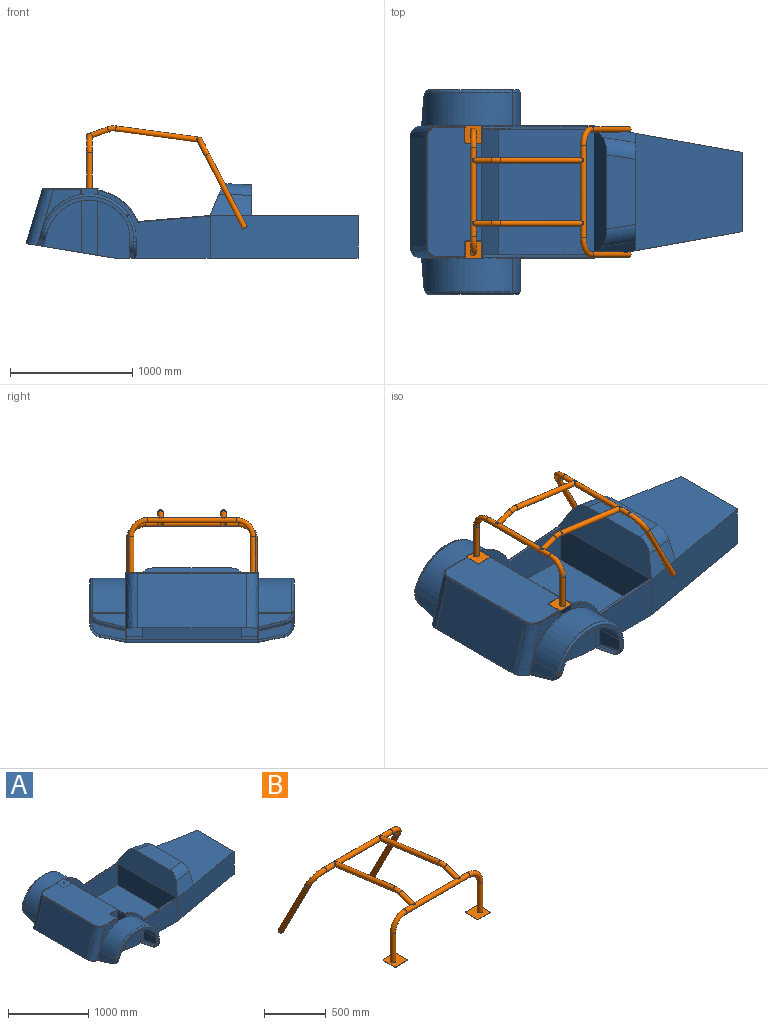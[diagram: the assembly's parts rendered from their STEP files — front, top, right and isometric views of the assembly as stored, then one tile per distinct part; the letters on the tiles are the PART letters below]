
ASSEMBLY  parts=2 mates=1
PART A: 180 faces, bbox 2842.1x1692.5x1027.8 mm
  f0: plane 10x10mm, normal (-1,0,0), area 21.5mm2, adj f1,f4,f161
  f1: plane 1374.1x570mm, normal (0,1,0), area 236734.2mm2, adj f0,f3,f4,f5,f11,f12,f15,f17
  f2: cylinder r=2.5mm len=25mm, axis (0,0,1), area 392.7mm2, adj f3,f4
  f3: plane 135x135mm, normal (0,0,-1), area 18205.4mm2, adj f1,f2,f5,f137,f138
  f4: plane 1070x442.56mm, normal (0,0,1), area 450483.3mm2, adj f0,f1,f2,f136,f139,f140,f161,f162
  f5: plane 498.97x135mm, normal (1,0,0), area 67361.3mm2, adj f1,f3,f16,f20,f138
  f6: cylinder r=350mm len=617.19mm, axis (0,1,0), area 3102.4mm2, adj f7,f10,f19,f30,f44,f57
  f7: cylinder r=363.11mm len=6.49mm, axis (0,1,0), area 32mm2, adj f6,f8,f19,f44
  f8: cylinder r=270mm len=155.14mm, axis (0,1,0), area 661.1mm2, adj f7,f14,f19,f44
  f9: plane 274.45x116.01mm, normal (-0.96,0,0.29), area 23220.8mm2, adj f15,f31,f32,f145
  f10: plane 289.56x128.37mm, normal (0.96,0,-0.29), area 1360.6mm2, adj f6,f16,f24,f29,f30,f41,f56,f57
  f11: plane 1985x1090mm, normal (0,0,-1), area 1885188.1mm2, adj f1,f16,f24,f26,f28,f61,f97,f99
  f12: plane 275x151.07mm, normal (1,0,0), area 33172.1mm2, adj f1,f13,f17,f27,f28
  f13: cylinder r=20mm len=30.73mm, axis (0,0,-1), area 965.5mm2, adj f12,f19,f23,f27
  f14: plane 290x170.47mm, normal (-1,0,0), area 1514.6mm2, adj f8,f19,f24,f25,f26,f44,f52,f53
  f15: cylinder r=400mm len=705.36mm, axis (0,-1,0), area 243757.5mm2, adj f1,f9,f18,f20,f21,f33
  f16: plane 1142.4x730mm, normal (-0.16,0,-0.99), area 20183mm2, adj f5,f10,f11,f20,f24,f29,f31,f81
  f17: cylinder r=320mm len=275mm, axis (0,-1,0), area 53866.2mm2, adj f1,f12,f18,f23
  f18: cylinder r=413.11mm len=275mm, axis (0,-1,0), area 2502.2mm2, adj f1,f15,f17,f22
  f19: plane 726.81x365mm, normal (0,1,0), area 30389.1mm2, adj f6,f7,f8,f13,f14,f21,f22,f23
  f20: plane 500.9x135mm, normal (0,-1,0), area 65864mm2, adj f5,f15,f16,f137
  f21: torus R=380mm, axis (0,1,0), area 27036.4mm2, adj f15,f19,f22,f33
  f22: torus R=393.11mm, axis (0,1,0), area 280.8mm2, adj f18,f19,f21,f23
  f23: torus R=300mm, axis (0,1,0), area 6013.9mm2, adj f13,f17,f19,f22
  f24: plane 709.39x474.73mm, normal (0,1,0), area 251490.4mm2, adj f10,f11,f14,f16,f35,f39,f49,f50
  f25: cylinder r=100mm len=98.08mm, axis (-1,0,0), area 4123.6mm2, adj f14,f19,f26,f27
  f26: plane 209.5x41.65mm, normal (0,0.2,-0.98), area 6408.1mm2, adj f11,f14,f25,f28
  f27: torus R=80mm, axis (1,0,0), area 4004.4mm2, adj f12,f13,f25,f28
  f28: cylinder r=20mm len=218.21mm, axis (0,0.98,0.2), area 6804mm2, adj f1,f11,f12,f26,f27
  f29: plane 203.47x52.98mm, normal (-0.28,0.24,-0.93), area 6044.2mm2, adj f10,f16,f30,f31
  f30: cylinder r=100mm len=101.65mm, axis (0.96,0,-0.29), area 3986.8mm2, adj f6,f10,f19,f29,f32,f33
  f31: cylinder r=20mm len=223.14mm, axis (0.07,0.97,0.23), area 6930.7mm2, adj f9,f16,f29,f32,f141
  f32: torus R=80mm, axis (-0.96,0,0.29), area 3529.2mm2, adj f9,f30,f31,f33
  f33: bspline ~41x29.86mm, area 352.5mm2, adj f15,f21,f30,f32
  f34: plane 270.45x115.06mm, normal (0.96,0,-0.29), area 22738.3mm2, adj f40,f45,f58,f59
  f35: plane 124.5x37.35mm, normal (-0.96,0,0.29), area 130mm2, adj f24,f41,f45,f51
  f36: plane 31.94x0.61mm, normal (0,0,1), area 19mm2, adj f39,f45,f53,f55
  f37: plane 271x150.28mm, normal (-1,0,0), area 32569.4mm2, adj f38,f42,f45,f54,f55
  f38: cylinder r=16mm len=30.73mm, axis (0,0,-1), area 772.4mm2, adj f37,f44,f48,f54
  f39: plane 166.47x1mm, normal (1,0,0), area 166.5mm2, adj f24,f36,f45,f49,f53
  f40: cylinder r=396mm len=698.31mm, axis (0,-1,0), area 237809.8mm2, adj f34,f43,f45,f46,f60
  f41: plane 37.09x26.85mm, normal (0.16,0,0.99), area 624.6mm2, adj f10,f35,f45,f56,f58
  f42: cylinder r=316mm len=271mm, axis (0,-1,0), area 52419.2mm2, adj f37,f43,f45,f48
  f43: cylinder r=409.11mm len=271mm, axis (0,-1,0), area 2442mm2, adj f40,f42,f45,f47
  f44: plane 726.81x365mm, normal (0,-1,0), area 30389.1mm2, adj f6,f7,f8,f14,f38,f46,f47,f48
  f45: plane 796.18x516.73mm, normal (0,1,0), area 60341.2mm2, adj f34,f35,f36,f37,f39,f40,f41,f42
  f46: torus R=380mm, axis (0,1,0), area 21488.9mm2, adj f40,f44,f47,f60
  f47: torus R=393.11mm, axis (0,1,0), area 223.3mm2, adj f43,f44,f46,f48
  f48: torus R=300mm, axis (0,1,0), area 4771.9mm2, adj f38,f42,f44,f47
  f49: cylinder r=270mm len=155.14mm, axis (0,1,0), area 165.3mm2, adj f24,f39,f45,f50
  f50: cylinder r=363.11mm len=6.49mm, axis (0,1,0), area 8mm2, adj f24,f45,f49,f51
  f51: cylinder r=350mm len=617.19mm, axis (0,1,0), area 775.6mm2, adj f24,f35,f45,f50
  f52: cylinder r=96mm len=94.16mm, axis (-1,0,0), area 3958.6mm2, adj f14,f44,f53,f54
  f53: plane 209.11x41.58mm, normal (0,-0.2,0.98), area 6396.2mm2, adj f14,f36,f39,f52,f55
  f54: torus R=80mm, axis (1,0,0), area 3115.5mm2, adj f37,f38,f52,f55
  f55: cylinder r=16mm len=212.82mm, axis (0,0.98,0.2), area 5344.2mm2, adj f36,f37,f45,f53,f54
  f56: plane 202.86x52.84mm, normal (0.28,-0.24,0.93), area 6025.4mm2, adj f10,f41,f57,f58
  f57: cylinder r=96mm len=97.93mm, axis (0.96,0,-0.29), area 3827.3mm2, adj f6,f10,f44,f56,f59,f60
  f58: cylinder r=16mm len=217.4mm, axis (0.07,0.97,0.23), area 5451mm2, adj f34,f41,f45,f56,f59
  f59: torus R=80mm, axis (-0.96,0,0.29), area 2745.8mm2, adj f34,f57,f58,f60
  f60: bspline ~38.29x25.61mm, area 272.9mm2, adj f40,f46,f57,f59
  f61: plane 920x570mm, normal (0,-1,0), area 208720.6mm2, adj f11,f73,f74,f75,f76,f87,f90,f91
  f62: cylinder r=440mm len=280.56mm, axis (0,-1,0), area 6757.6mm2, adj f63,f71,f76,f136
  f63: cylinder r=453.11mm len=20mm, axis (0,-1,0), area 199.6mm2, adj f62,f64,f71,f75
  f64: cylinder r=360mm len=77.32mm, axis (0,-1,0), area 1757.2mm2, adj f63,f65,f71,f74
  f65: plane 589.44x50mm, normal (-0.08,0,1), area 11831mm2, adj f64,f71,f73,f174
  f66: cylinder r=440mm len=280.56mm, axis (0,-1,0), area 6757.6mm2, adj f67,f72,f77,f136
  f67: cylinder r=453.11mm len=20mm, axis (0,-1,0), area 199.6mm2, adj f66,f68,f72,f78
  f68: cylinder r=360mm len=77.32mm, axis (0,-1,0), area 1757.2mm2, adj f67,f69,f72,f80
  f69: plane 589.44x50mm, normal (-0.08,0,1), area 11831mm2, adj f68,f72,f79,f174
  f70: plane 1030x781.36mm, normal (0,0,1), area 804800.4mm2, adj f71,f72,f136,f166
  f71: plane 917.07x533.49mm, normal (0,1,0), area 288293.1mm2, adj f62,f63,f64,f65,f70,f136,f166
  f72: plane 917.07x533.49mm, normal (0,-1,0), area 288293.1mm2, adj f66,f67,f68,f69,f70,f136,f166
  f73: cylinder r=5mm len=593.62mm, axis (1,0,0.08), area 4655.6mm2, adj f61,f65,f74,f169
  f74: torus R=355mm, axis (0,1,0), area 697.3mm2, adj f61,f64,f73,f75
  f75: torus R=448.11mm, axis (0,1,0), area 78.1mm2, adj f61,f63,f74,f76
  f76: torus R=435mm, axis (0,1,0), area 2636.4mm2, adj f61,f62,f75,f136
  f77: torus R=435mm, axis (0,1,0), area 2636.4mm2, adj f1,f66,f78,f136
  f78: torus R=448.11mm, axis (0,1,0), area 78.1mm2, adj f1,f67,f77,f80
  f79: cylinder r=5mm len=593.62mm, axis (-1,0,-0.08), area 4655.6mm2, adj f1,f69,f80,f167
  f80: torus R=355mm, axis (0,1,0), area 697.3mm2, adj f1,f68,f78,f79
  f81: plane 500.9x135mm, normal (0,1,0), area 65864mm2, adj f16,f90,f135,f140
  f82: cylinder r=350mm len=617.19mm, axis (0,-1,0), area 3102.4mm2, adj f83,f86,f93,f103,f117,f130
  f83: cylinder r=363.11mm len=6.49mm, axis (0,-1,0), area 32mm2, adj f82,f84,f93,f117
  f84: cylinder r=270mm len=155.14mm, axis (0,-1,0), area 661.1mm2, adj f83,f89,f93,f117
  f85: plane 274.45x116.01mm, normal (-0.96,0,0.29), area 23220.8mm2, adj f90,f104,f105,f143
  f86: plane 289.56x128.37mm, normal (0.96,0,-0.29), area 1360.6mm2, adj f16,f82,f97,f102,f103,f114,f129,f130
  f87: plane 275x151.07mm, normal (1,0,0), area 33172.1mm2, adj f61,f88,f91,f100,f101
  f88: cylinder r=20mm len=30.73mm, axis (0,0,-1), area 965.5mm2, adj f87,f93,f96,f100
  f89: plane 290x170.47mm, normal (-1,0,0), area 1514.6mm2, adj f84,f93,f97,f98,f99,f117,f125,f126
  f90: cylinder r=400mm len=705.36mm, axis (0,1,0), area 243757.5mm2, adj f61,f81,f85,f92,f94,f106,f134
  f91: cylinder r=320mm len=275mm, axis (0,1,0), area 53866.2mm2, adj f61,f87,f92,f96
  f92: cylinder r=413.11mm len=275mm, axis (0,1,0), area 2502.2mm2, adj f61,f90,f91,f95
  f93: plane 726.81x365mm, normal (0,-1,0), area 30389.1mm2, adj f82,f83,f84,f88,f89,f94,f95,f96
  f94: torus R=380mm, axis (0,-1,0), area 27036.4mm2, adj f90,f93,f95,f106
  f95: torus R=393.11mm, axis (0,-1,0), area 280.8mm2, adj f92,f93,f94,f96
  f96: torus R=300mm, axis (0,-1,0), area 6013.9mm2, adj f88,f91,f93,f95
  f97: plane 709.39x474.73mm, normal (0,-1,0), area 251490.4mm2, adj f11,f16,f86,f89,f108,f112,f122,f123
  f98: cylinder r=100mm len=98.08mm, axis (-1,0,0), area 4123.6mm2, adj f89,f93,f99,f100
  f99: plane 209.5x41.65mm, normal (0,-0.2,-0.98), area 6408.1mm2, adj f11,f89,f98,f101
  f100: torus R=80mm, axis (1,0,0), area 4004.4mm2, adj f87,f88,f98,f101
  f101: cylinder r=20mm len=218.21mm, axis (0,-0.98,0.2), area 6804mm2, adj f11,f61,f87,f99,f100
  f102: plane 203.47x52.98mm, normal (-0.28,-0.24,-0.93), area 6044.2mm2, adj f16,f86,f103,f104
  f103: cylinder r=100mm len=101.65mm, axis (0.96,0,-0.29), area 3986.8mm2, adj f82,f86,f93,f102,f105,f106
  f104: cylinder r=20mm len=223.14mm, axis (0.07,-0.97,0.23), area 6930.7mm2, adj f16,f85,f102,f105,f142
  f105: torus R=80mm, axis (-0.96,0,0.29), area 3529.2mm2, adj f85,f103,f104,f106
  f106: bspline ~41x29.86mm, area 352.5mm2, adj f90,f94,f103,f105
  f107: plane 270.45x115.06mm, normal (0.96,0,-0.29), area 22738.3mm2, adj f113,f118,f131,f132
  f108: plane 124.5x37.35mm, normal (-0.96,0,0.29), area 130mm2, adj f97,f114,f118,f124
  f109: plane 31.94x0.61mm, normal (0,0,1), area 19mm2, adj f112,f118,f126,f128
  f110: plane 271x150.28mm, normal (-1,0,0), area 32569.4mm2, adj f111,f115,f118,f127,f128
  f111: cylinder r=16mm len=30.73mm, axis (0,0,-1), area 772.4mm2, adj f110,f117,f121,f127
  f112: plane 166.47x1mm, normal (1,0,0), area 166.5mm2, adj f97,f109,f118,f122,f126
  f113: cylinder r=396mm len=698.31mm, axis (0,1,0), area 237809.8mm2, adj f107,f116,f118,f119,f133
  f114: plane 37.09x26.85mm, normal (0.16,0,0.99), area 624.6mm2, adj f86,f108,f118,f129,f131
  f115: cylinder r=316mm len=271mm, axis (0,1,0), area 52419.2mm2, adj f110,f116,f118,f121
  f116: cylinder r=409.11mm len=271mm, axis (0,1,0), area 2442mm2, adj f113,f115,f118,f120
  f117: plane 726.81x365mm, normal (0,1,0), area 30389.1mm2, adj f82,f83,f84,f89,f111,f119,f120,f121
  f118: plane 796.18x516.73mm, normal (0,-1,0), area 60341.2mm2, adj f107,f108,f109,f110,f112,f113,f114,f115
  f119: torus R=380mm, axis (0,-1,0), area 21488.9mm2, adj f113,f117,f120,f133
  f120: torus R=393.11mm, axis (0,-1,0), area 223.3mm2, adj f116,f117,f119,f121
  f121: torus R=300mm, axis (0,-1,0), area 4771.9mm2, adj f111,f115,f117,f120
  f122: cylinder r=270mm len=155.14mm, axis (0,-1,0), area 165.3mm2, adj f97,f112,f118,f123
  f123: cylinder r=363.11mm len=6.49mm, axis (0,-1,0), area 8mm2, adj f97,f118,f122,f124
  f124: cylinder r=350mm len=617.19mm, axis (0,-1,0), area 775.6mm2, adj f97,f108,f118,f123
  f125: cylinder r=96mm len=94.16mm, axis (-1,0,0), area 3958.6mm2, adj f89,f117,f126,f127
  f126: plane 209.11x41.58mm, normal (0,0.2,0.98), area 6396.2mm2, adj f89,f109,f112,f125,f128
  f127: torus R=80mm, axis (1,0,0), area 3115.5mm2, adj f110,f111,f125,f128
  f128: cylinder r=16mm len=212.82mm, axis (0,-0.98,0.2), area 5344.2mm2, adj f109,f110,f118,f126,f127
  f129: plane 202.86x52.84mm, normal (0.28,0.24,0.93), area 6025.4mm2, adj f86,f114,f130,f131
  f130: cylinder r=96mm len=97.93mm, axis (0.96,0,-0.29), area 3827.3mm2, adj f82,f86,f117,f129,f132,f133
  f131: cylinder r=16mm len=217.4mm, axis (0.07,-0.97,0.23), area 5451mm2, adj f107,f114,f118,f129,f132
  f132: torus R=80mm, axis (-0.96,0,0.29), area 2745.8mm2, adj f107,f130,f131,f133
  f133: bspline ~38.29x25.61mm, area 272.9mm2, adj f113,f119,f130,f132
  f134: plane 320.33x319.1mm, normal (0,-1,0), area 24638.7mm2, adj f90,f140,f143,f165
  f135: plane 546.16x135mm, normal (-1,0,0), area 73732.2mm2, adj f16,f61,f81,f136,f139
  f136: plane 1080x545mm, normal (0.97,0,0.25), area 579834.2mm2, adj f1,f4,f61,f62,f66,f70,f71,f72
  f137: plane 521.16x135mm, normal (-1,0,0), area 70357.2mm2, adj f1,f3,f16,f20,f138
  f138: plane 521.16x135mm, normal (0,1,0), area 68859.2mm2, adj f3,f5,f16,f137
  f139: plane 546.16x135mm, normal (0,-1,0), area 72234.2mm2, adj f4,f16,f135,f140
  f140: plane 523.97x135mm, normal (1,0,0), area 70714.8mm2, adj f4,f16,f81,f134,f139,f165
  f141: plane 20.24x10.28mm, normal (0,1,0), area 60.7mm2, adj f16,f31,f145
  f142: plane 20.24x10.28mm, normal (0,-1,0), area 60.7mm2, adj f16,f104,f143
  f143: bspline ~457.76x232.33mm, area 68212.1mm2, adj f16,f85,f134,f142,f144,f164
  f144: plane 890x442.87mm, normal (-0.96,0,0.29), area 411512.4mm2, adj f16,f143,f145,f163
  f145: bspline ~457.76x232.33mm, area 68212.1mm2, adj f1,f9,f16,f141,f144,f162
  f146: plane 1074x445.44mm, normal (0,0,-1), area 438139.8mm2, adj f147,f149,f151,f152,f153,f154,f155,f156
  f147: plane 520.48x135mm, normal (-1,0,0), area 70264.7mm2, adj f16,f146,f151,f154
  f148: plane 522.7x135mm, normal (1,0,0), area 70563.9mm2, adj f16,f149,f152,f160
  f149: plane 1074x566.47mm, normal (-0.97,0,-0.25), area 621924.2mm2, adj f16,f146,f148,f150,f151,f152,f159,f160
  f150: plane 522.7x135mm, normal (1,0,0), area 70563.9mm2, adj f16,f149,f151,f159
  f151: plane 543.66x141mm, normal (0,-1,0), area 74965.8mm2, adj f16,f146,f147,f149,f150
  f152: plane 543.66x141mm, normal (0,1,0), area 74965.8mm2, adj f16,f146,f148,f149,f153
  f153: plane 520.48x135mm, normal (-1,0,0), area 70264.7mm2, adj f16,f146,f152,f155
  f154: plane 520.48x356.46mm, normal (0,-1,0), area 143088.4mm2, adj f16,f146,f147,f158
  f155: plane 520.48x356.46mm, normal (0,1,0), area 143088.4mm2, adj f16,f146,f153,f156
  f156: offset ~1027.76x407.53mm, area 66815.4mm2, adj f16,f146,f155,f157
  f157: plane 890x447.49mm, normal (0.96,0,-0.29), area 415802.6mm2, adj f16,f146,f156,f158
  f158: offset ~1027.76x407.53mm, area 66815.5mm2, adj f16,f146,f154,f157
  f159: plane 545.51x138.77mm, normal (0,-1,0), area 36267.1mm2, adj f16,f149,f150
  f160: plane 545.51x138.77mm, normal (0,1,0), area 36267.1mm2, adj f16,f148,f149
  f161: cylinder r=10mm len=223mm, axis (1,0,0), area 3502.9mm2, adj f0,f1,f4,f162
  f162: bspline ~120.72x94.19mm, area 1969.7mm2, adj f4,f145,f161,f163
  f163: cylinder r=10mm len=890mm, axis (0,1,0), area 11386.1mm2, adj f4,f144,f162,f164
  f164: bspline ~121.06x94.34mm, area 1969.7mm2, adj f4,f143,f163,f165
  f165: cylinder r=10mm len=223mm, axis (-1,0,0), area 3502.9mm2, adj f4,f134,f140,f164
  f166: plane 1030x325mm, normal (-1,0,0), area 334750mm2, adj f70,f71,f72,f174
  f167: plane 5.02x5mm, normal (-1,0,0), area 5.4mm2, adj f79,f168,f174
  f168: plane 1210x350mm, normal (0.17,0.98,0), area 430133.5mm2, adj f1,f11,f167,f171,f172,f178
  f169: plane 5.02x5mm, normal (-1,0,0), area 5.4mm2, adj f73,f170,f174
  f170: plane 1210x350mm, normal (0.17,-0.98,0), area 430133.5mm2, adj f11,f61,f169,f171,f172,f176
  f171: plane 650x350mm, normal (1,0,0), area 227500mm2, adj f11,f168,f170,f172
  f172: plane 959.17x870mm, normal (0,0,1), area 699990.5mm2, adj f168,f170,f171,f173
  f173: plane 959.17x250mm, normal (1,0,0), area 207339.1mm2, adj f172,f175,f176,f177,f178,f179
  f174: plane 1080x260mm, normal (-0.93,0,0.37), area 260080.4mm2, adj f65,f69,f166,f167,f169,f175,f176,f177
  f175: plane 606.11x235mm, normal (0.04,0,1), area 133844.8mm2, adj f173,f174,f177,f179
  f176: plane 340x175.2mm, normal (0.16,-0.89,0.42), area 57974.3mm2, adj f170,f173,f174,f177
  f177: cylinder r=150mm len=304.15mm, axis (0.99,0.16,-0.04), area 42459.5mm2, adj f173,f174,f175,f176
  f178: plane 340x175.2mm, normal (0.16,0.89,0.42), area 57974.3mm2, adj f168,f173,f174,f179
  f179: cylinder r=150mm len=304.15mm, axis (0.99,-0.16,-0.04), area 42459.5mm2, adj f173,f174,f175,f178
PART B: 88 faces, bbox 1095x1362.7x859.4 mm
  f0: cylinder r=22.5mm len=725mm, axis (-1,0,0), area 98445.6mm2, adj f2,f3,f55,f56
  f1: cylinder r=22.5mm len=289.5mm, axis (0,0,1), area 40927.1mm2, adj f2,f5
  f2: torus R=135mm, axis (0,-1,0), area 29978.9mm2, adj f0,f1
  f3: torus R=135mm, axis (0,-1,0), area 29978.9mm2, adj f0,f4
  f4: cylinder r=22.5mm len=289.5mm, axis (0,0,-1), area 40927.1mm2, adj f3,f15
  f5: plane 145x145mm, normal (0,0,1), area 19348.7mm2, adj f1,f6,f7,f8,f9,f10,f11,f12
  f6: cylinder r=10mm len=10mm, axis (0,0,-1), area 47.1mm2, adj f5,f7,f13,f14
  f7: plane 125x3mm, normal (0,-1,0), area 375mm2, adj f5,f6,f8,f14
  f8: cylinder r=10mm len=10mm, axis (0,0,-1), area 47.1mm2, adj f5,f7,f9,f14
  f9: plane 125x3mm, normal (-1,0,0), area 375mm2, adj f5,f8,f10,f14
  f10: cylinder r=10mm len=10mm, axis (0,0,-1), area 47.1mm2, adj f5,f9,f11,f14
  f11: plane 125x3mm, normal (0,1,0), area 375mm2, adj f5,f10,f12,f14
  f12: cylinder r=10mm len=10mm, axis (0,0,-1), area 47.1mm2, adj f5,f11,f13,f14
  f13: plane 125x3mm, normal (1,0,0), area 375mm2, adj f5,f6,f12,f14
  f14: plane 145x145mm, normal (0,0,-1), area 20939.2mm2, adj f6,f7,f8,f9,f10,f11,f12,f13
  f15: plane 145x145mm, normal (0,0,1), area 19348.7mm2, adj f4,f16,f17,f18,f19,f20,f21,f22
  f16: plane 125x3mm, normal (1,0,0), area 375mm2, adj f15,f17,f23,f24
  f17: cylinder r=10mm len=10mm, axis (0,0,-1), area 47.1mm2, adj f15,f16,f18,f24
  f18: plane 125x3mm, normal (0,-1,0), area 375mm2, adj f15,f17,f19,f24
  f19: cylinder r=10mm len=10mm, axis (0,0,-1), area 47.1mm2, adj f15,f18,f20,f24
  f20: plane 125x3mm, normal (-1,0,0), area 375mm2, adj f15,f19,f21,f24
  f21: cylinder r=10mm len=10mm, axis (0,0,-1), area 47.1mm2, adj f15,f20,f22,f24
  f22: plane 125x3mm, normal (0,1,0), area 375mm2, adj f15,f21,f23,f24
  f23: cylinder r=10mm len=10mm, axis (0,0,-1), area 47.1mm2, adj f15,f16,f22,f24
  f24: plane 145x145mm, normal (0,0,-1), area 20939.2mm2, adj f16,f17,f18,f19,f20,f21,f22,f23
  f25: cylinder r=20mm len=40.14mm, axis (1,0,0), area 1600mm2, adj f26,f29
  f26: cylinder r=20mm len=42.32mm, axis (0,0.99,-0.13), area 800mm2, adj f25,f27
  f27: plane 39.64x22.5mm, normal (0,0.99,-0.13), area 132.1mm2, adj f26,f28,f32
  f28: cylinder r=22.5mm len=42.31mm, axis (0,0.99,-0.13), area 724.9mm2, adj f27,f32
  f29: cylinder r=20mm len=42.32mm, axis (0,0.99,-0.13), area 800mm2, adj f25,f30
  f30: plane 39.64x22.5mm, normal (0,0.99,-0.13), area 132.1mm2, adj f29,f31,f32
  f31: cylinder r=22.5mm len=42.31mm, axis (0,0.99,-0.13), area 724.9mm2, adj f30,f32
  f32: cylinder r=20mm len=754mm, axis (1,0,0), area 90484.1mm2, adj f27,f28,f30,f31,f43,f44,f46,f47
  f33: torus R=135mm, axis (-1,0,0), area 9130mm2, adj f34,f55
  f34: cylinder r=22.5mm len=688.48mm, axis (0,0.99,-0.13), area 95329.4mm2, adj f33,f37
  f35: cylinder r=22.5mm len=620.93mm, axis (0,0.46,-0.89), area 95425.9mm2, adj f36,f40
  f36: torus R=135mm, axis (0,0.89,0.46), area 29978.9mm2, adj f35,f37
  f37: cylinder r=22.5mm len=754mm, axis (1,0,0), area 102544.2mm2, adj f34,f36,f38,f54
  f38: torus R=135mm, axis (0,0.89,0.46), area 29978.9mm2, adj f37,f39
  f39: cylinder r=22.5mm len=620.93mm, axis (0,-0.46,0.89), area 95425.9mm2, adj f38,f41
  f40: plane 45x40.02mm, normal (0,0.46,-0.89), area 333.8mm2, adj f35,f42
  f41: plane 45x40.02mm, normal (0,0.46,-0.89), area 333.8mm2, adj f39,f45
  f42: cylinder r=20mm len=618.65mm, axis (0,0.46,-0.89), area 84823mm2, adj f40,f43
  f43: torus R=135mm, axis (0,0.89,0.46), area 26647.9mm2, adj f32,f42
  f44: torus R=135mm, axis (0,0.89,0.46), area 26647.9mm2, adj f32,f45
  f45: cylinder r=20mm len=618.65mm, axis (0,-0.46,0.89), area 84823mm2, adj f41,f44
  f46: cylinder r=22.5mm len=42.31mm, axis (0,0.99,-0.13), area 724.9mm2, adj f32,f47
  f47: plane 39.64x22.5mm, normal (0,0.99,-0.13), area 132.1mm2, adj f32,f46,f48
  f48: cylinder r=20mm len=42.32mm, axis (0,0.99,-0.13), area 800mm2, adj f47,f52
  f49: cylinder r=22.5mm len=42.31mm, axis (0,0.99,-0.13), area 724.9mm2, adj f32,f50
  f50: plane 39.64x22.5mm, normal (0,0.99,-0.13), area 132.1mm2, adj f32,f49,f51
  f51: cylinder r=20mm len=42.32mm, axis (0,0.99,-0.13), area 800mm2, adj f50,f52
  f52: cylinder r=20mm len=40.14mm, axis (1,0,0), area 1600mm2, adj f48,f51
  f53: torus R=135mm, axis (-1,0,0), area 9130mm2, adj f54,f56
  f54: cylinder r=22.5mm len=688.48mm, axis (0,0.99,-0.13), area 95329.4mm2, adj f37,f53
  f55: cylinder r=22.5mm len=169.11mm, axis (0,0.94,0.34), area 21092.1mm2, adj f0,f33
  f56: cylinder r=22.5mm len=169.11mm, axis (0,0.94,0.34), area 21092.1mm2, adj f0,f53
  f57: cylinder r=22.5mm len=40mm, axis (1,0,0), area 1448.7mm2, adj f58
  f58: cylinder r=20mm len=677.6mm, axis (0,0.99,-0.13), area 84403.6mm2, adj f57,f59
  f59: torus R=135mm, axis (-1,0,0), area 8115.6mm2, adj f58,f60
  f60: cylinder r=20mm len=157.72mm, axis (0,0.94,0.34), area 18414.4mm2, adj f59,f61
  f61: cylinder r=22.5mm len=40mm, axis (-1,0,0), area 1448.7mm2, adj f60
  f62: cylinder r=20mm len=725mm, axis (-1,0,0), area 86839.8mm2, adj f66,f67,f70,f71,f74,f75,f76,f77
  f63: plane 40x40mm, normal (0,0,1), area 1256.6mm2, adj f68
  f64: plane 40x40mm, normal (0,0,1), area 1256.6mm2, adj f65
  f65: cylinder r=20mm len=289.5mm, axis (0,0,1), area 36379.6mm2, adj f64,f66
  f66: torus R=135mm, axis (0,-1,0), area 26647.9mm2, adj f62,f65
  f67: torus R=135mm, axis (0,-1,0), area 26647.9mm2, adj f62,f68
  f68: cylinder r=20mm len=289.5mm, axis (0,0,-1), area 36379.6mm2, adj f63,f67
  f69: cylinder r=20mm len=44.43mm, axis (0,0.94,0.34), area 800mm2, adj f70,f72
  f70: plane 37.65x22.5mm, normal (0,-0.94,-0.34), area 132.1mm2, adj f62,f69,f71
  f71: cylinder r=22.5mm len=44.4mm, axis (0,0.94,0.34), area 724.9mm2, adj f62,f70
  f72: cylinder r=20mm len=40.14mm, axis (-1,0,0), area 1600mm2, adj f69,f73
  f73: cylinder r=20mm len=44.43mm, axis (0,0.94,0.34), area 800mm2, adj f72,f74
  f74: plane 37.65x22.5mm, normal (0,-0.94,-0.34), area 132.1mm2, adj f62,f73,f75
  f75: cylinder r=22.5mm len=44.4mm, axis (0,0.94,0.34), area 724.9mm2, adj f62,f74
  f76: cylinder r=22.5mm len=44.4mm, axis (0,0.94,0.34), area 724.9mm2, adj f62,f77
  f77: plane 37.65x22.5mm, normal (0,-0.94,-0.34), area 132.1mm2, adj f62,f76,f78
  f78: cylinder r=20mm len=44.43mm, axis (0,0.94,0.34), area 800mm2, adj f77,f82
  f79: cylinder r=22.5mm len=44.4mm, axis (0,0.94,0.34), area 724.9mm2, adj f62,f80
  f80: plane 37.65x22.5mm, normal (0,-0.94,-0.34), area 132.1mm2, adj f62,f79,f81
  f81: cylinder r=20mm len=44.43mm, axis (0,0.94,0.34), area 800mm2, adj f80,f82
  f82: cylinder r=20mm len=40.14mm, axis (-1,0,0), area 1600mm2, adj f78,f81
  f83: cylinder r=20mm len=157.72mm, axis (0,0.94,0.34), area 18414.4mm2, adj f85,f87
  f84: cylinder r=20mm len=677.6mm, axis (0,0.99,-0.13), area 84403.6mm2, adj f85,f86
  f85: torus R=135mm, axis (-1,0,0), area 8115.6mm2, adj f83,f84
  f86: cylinder r=22.5mm len=40mm, axis (1,0,0), area 1448.7mm2, adj f84
  f87: cylinder r=22.5mm len=40mm, axis (-1,0,0), area 1448.7mm2, adj f83
PLACE A at identity
PLACE B rot(axis=(0,0,-1),90deg) t=(-67.5,0,730)mm
MATE parallel B.f24 <-> A.f2  axis (0,0,-1) through (-67.5,472.5,730)mm
